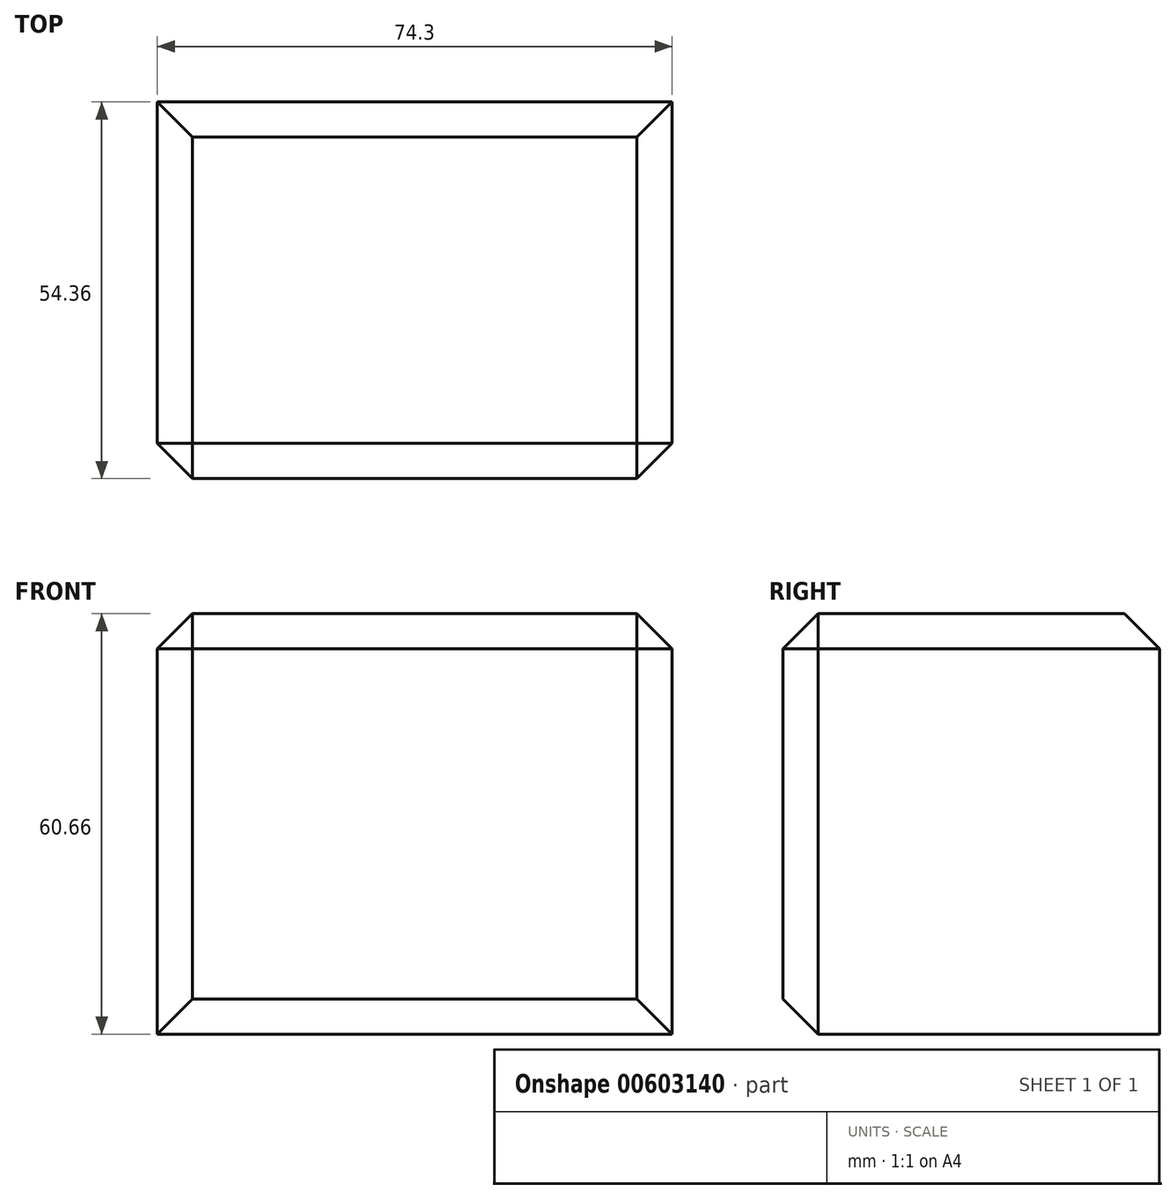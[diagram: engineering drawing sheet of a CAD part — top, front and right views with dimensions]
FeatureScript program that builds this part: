
annotation { "Feature Type Name" : "Feature", "Feature Type Description" : "" }
export const myFeature = defineFeature(function(context is Context, id is Id, definition is map)
    precondition{}
    {
        {
            var Q0;
            Q0=qCreatedBy(makeId("Front.planeOp"),FACE);
            var sketch = newSketch(context, id + "F0", { "sketchPlane" : qUnion([Q0])});
            skLineSegment(sketch, "E0.bottom", {"start": v(37.15, 30.33) * mm, "end": v(-37.15, 30.33) * mm});
            skLineSegment(sketch, "E0.top", {"start": v(37.15, -30.33) * mm, "end": v(-37.15, -30.33) * mm});
            skLineSegment(sketch, "E0.left", {"start": v(37.15, 30.33) * mm, "end": v(37.15, -30.33) * mm});
            skLineSegment(sketch, "E0.right", {"start": v(-37.15, 30.33) * mm, "end": v(-37.15, -30.33) * mm});
            skPoint(sketch, "E0.middle", {"position": v(0, 0) * mm});
            skSolve(sketch);
        }
        {
            var Q0;
            Q0 = qSketchRegion(id + "F0", true);
            extrude(context, id + "F1", {"entities" : qUnion([Q0]), "depth" : 54.36 * mm, "offsetDistance" : 25.4 * mm});
        }
        {
            var Q0;
            Q0=makeQuery(id+"F1.opExtrude","CAP_FACE",FACE,{"disambiguationData":[OSD([sQuery(id+"F0.wireOp",EDGE,"E0.bottom"),sQuery(id+"F0.wireOp",EDGE,"E0.top"),sQuery(id+"F0.wireOp",EDGE,"E0.left"),sQuery(id+"F0.wireOp",EDGE,"E0.right")])],"isStart":false});
            var Q1;
            Q1=makeQuery(id+"F1.opExtrude","SWEPT_FACE",FACE,{"disambiguationData":[OSD([sQuery(id+"F0.wireOp",EDGE,"E0.bottom")])]});
            chamfer(context, id + "F2", {"entities" : qUnion([Q0, Q1]), "chamferType" : ChamferType.TWO_OFFSETS, "width1" : 5.08 * mm, "oppositeDirection" : false, "width2" : 5.08 * mm, "tangentPropagation" : true});
        }
        {
            var Q0;
            Q0=makeQuery(id+"F1.opExtrude","SWEPT_FACE",FACE,{"disambiguationData":[OSD([sQuery(id+"F0.wireOp",EDGE,"E0.left")])]});
            var sketch = newSketch(context, id + "F3", { "sketchPlane" : qUnion([Q0])});
            skCircle(sketch, "E1", {"center": v(-23.25, 0) * mm, "radius": 6.41 * mm});
            skSolve(sketch);
        }
        {
            var Q0;
            Q0=sQuery(id+"F3.wireOp",EDGE,"E1");
            extrude(context, id + "F4", {"bodyType" : ToolBodyType.SURFACE, "surfaceEntities" : qUnion([Q0]), "oppositeDirection" : true, "depth" : 25.4 * mm, "offsetDistance" : 25.4 * mm});
        }
    });
